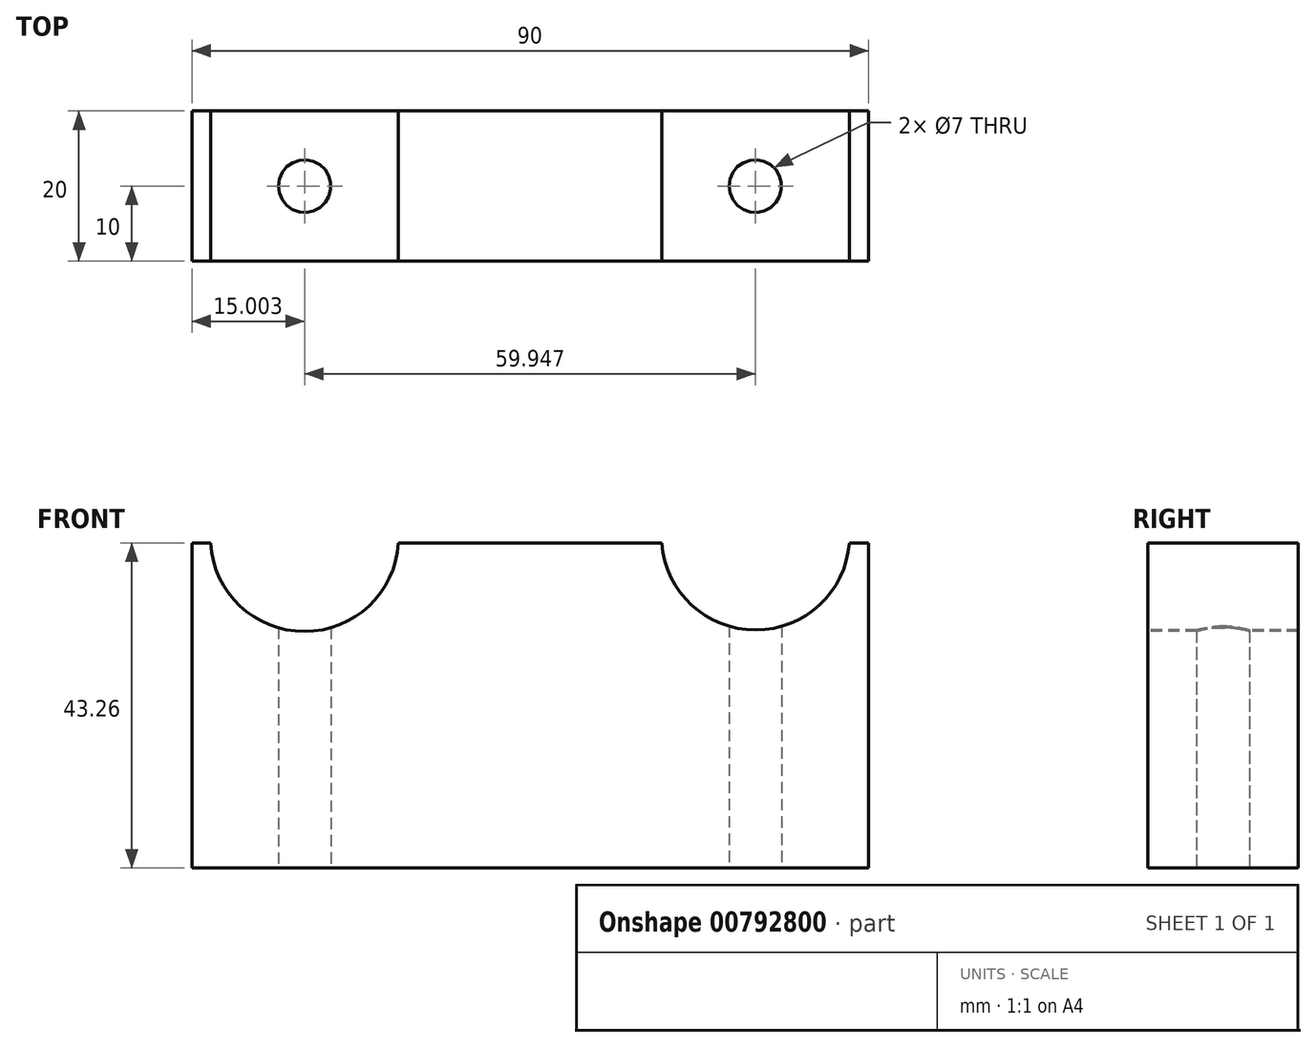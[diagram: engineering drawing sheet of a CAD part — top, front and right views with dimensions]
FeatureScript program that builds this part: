
annotation { "Feature Type Name" : "Feature", "Feature Type Description" : "" }
export const myFeature = defineFeature(function(context is Context, id is Id, definition is map)
    precondition{}
    {
        {
            var Q0;
            Q0=qCreatedBy(makeId("Front.planeOp"),FACE);
            var sketch = newSketch(context, id + "F0", { "sketchPlane" : qUnion([Q0])});
            skLineSegment(sketch, "E0.bottom", {"start": v(-45, 21.63) * mm, "end": v(45, 21.63) * mm});
            skLineSegment(sketch, "E0.top", {"start": v(-45, -21.62) * mm, "end": v(45, -21.62) * mm});
            skLineSegment(sketch, "E0.left", {"start": v(-45, 21.63) * mm, "end": v(-45, -21.62) * mm});
            skLineSegment(sketch, "E0.right", {"start": v(45, 21.63) * mm, "end": v(45, -21.62) * mm});
            skPoint(sketch, "E0.middle", {"position": v(0, 0) * mm});
            skSolve(sketch);
        }
        {
            var Q0;
            Q0 = qSketchRegion(id + "F0", true);
            extrude(context, id + "F1", {"entities" : qUnion([Q0]), "endBound" : BoundingType.SYMMETRIC, "depth" : 20 * mm, "offsetDistance" : 25.4 * mm});
        }
        {
            var Q0;
            Q0=qCreatedBy(makeId("Front.planeOp"),FACE);
            var sketch = newSketch(context, id + "F2", { "sketchPlane" : qUnion([Q0])});
            skCircle(sketch, "E1", {"center": v(-30.02, 22.33) * mm, "radius": 12.5 * mm});
            skCircle(sketch, "E2", {"center": v(29.98, 22.53) * mm, "radius": 12.5 * mm});
            skSolve(sketch);
        }
        {
            var Q0;
            Q0 = qSketchRegion(id + "F2", true);
            extrude(context, id + "F3", {"entities" : qUnion([Q0]), "operationType" : NewBodyOperationType.REMOVE, "endBound" : BoundingType.SYMMETRIC, "oppositeDirection" : true, "depth" : 30 * mm, "offsetDistance" : 25.4 * mm});
        }
        {
            var Q0;
            Q0=qCreatedBy(makeId("Top.planeOp"),FACE);
            var sketch = newSketch(context, id + "F4", { "sketchPlane" : qUnion([Q0])});
            skCircle(sketch, "E3", {"center": v(-30, 0) * mm, "radius": 3.5 * mm});
            skCircle(sketch, "E4", {"center": v(29.95, 0) * mm, "radius": 3.5 * mm});
            skSolve(sketch);
        }
        {
            var Q0;
            Q0 = qSketchRegion(id + "F4", true);
            extrude(context, id + "F5", {"entities" : qUnion([Q0]), "operationType" : NewBodyOperationType.REMOVE, "endBound" : BoundingType.SYMMETRIC, "depth" : 80 * mm, "offsetDistance" : 25.4 * mm});
        }
    });
